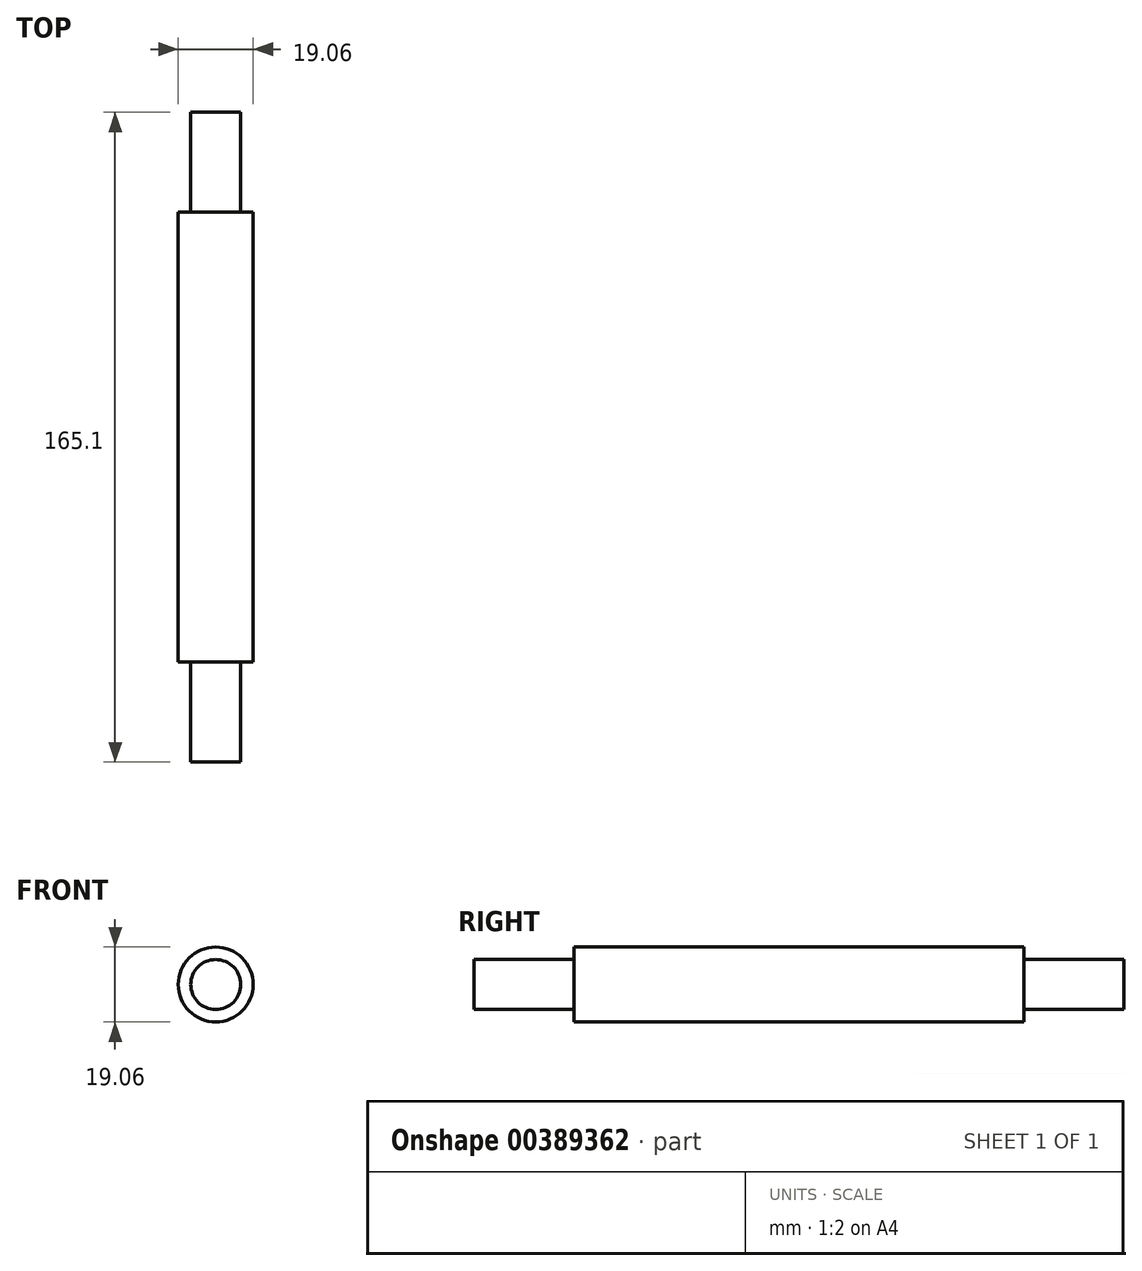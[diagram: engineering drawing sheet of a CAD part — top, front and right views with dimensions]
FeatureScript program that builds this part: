
annotation { "Feature Type Name" : "Feature", "Feature Type Description" : "" }
export const myFeature = defineFeature(function(context is Context, id is Id, definition is map)
    precondition{}
    {
        {
            var Q0;
            Q0=qCreatedBy(makeId("Front.planeOp"),FACE);
            var sketch = newSketch(context, id + "F0", { "sketchPlane" : qUnion([Q0])});
            skCircle(sketch, "E0", {"center": v(0, 0) * mm, "radius": 9.53 * mm});
            skSolve(sketch);
        }
        {
            var Q0;
            Q0=makeQuery(id+"F0.imprint","IMPRINT",FACE,{"disambiguationData":[TD([[makeQuery(id+"F0.imprint","IMPRINT",EDGE,{"derivedFrom":sQuery(id+"F0.wireOp",EDGE,"E0")}),1.0]])]});
            extrude(context, id + "F1", {"entities" : qUnion([Q0]), "depth" : 114.3 * mm});
        }
        {
            var Q0;
            Q0=makeQuery(id+"F1.opExtrude","CAP_FACE",FACE,{"disambiguationData":[OSD([sQuery(id+"F0.wireOp",EDGE,"E0")])],"isStart":false});
            var sketch = newSketch(context, id + "F2", { "sketchPlane" : qUnion([Q0])});
            skCircle(sketch, "E1", {"center": v(0, 0) * mm, "radius": 6.35 * mm});
            skSolve(sketch);
        }
        {
            var Q0;
            Q0 = qSketchRegion(id + "F2", true);
            extrude(context, id + "F3", {"entities" : qUnion([Q0]), "operationType" : NewBodyOperationType.ADD, "depth" : 25.4 * mm});
        }
        {
            var Q0;
            Q0=makeQuery(id+"F1.opExtrude","CAP_FACE",FACE,{"disambiguationData":[OSD([sQuery(id+"F0.wireOp",EDGE,"E0")])],"isStart":true});
            var sketch = newSketch(context, id + "F4", { "sketchPlane" : qUnion([Q0])});
            skCircle(sketch, "E2", {"center": v(0, 0) * mm, "radius": 6.35 * mm});
            skCircle(sketch, "E3", {"center": v(0, 0) * mm, "radius": 9.53 * mm});
            skSolve(sketch);
        }
        {
            var Q0;
            Q0=makeQuery(id+"F4.imprint","IMPRINT",FACE,{"disambiguationData":[TD([[makeQuery(id+"F4.imprint","IMPRINT",EDGE,{"derivedFrom":sQuery(id+"F4.wireOp",EDGE,"E2")}),1.0]])]});
            extrude(context, id + "F5", {"entities" : qUnion([Q0]), "operationType" : NewBodyOperationType.ADD, "depth" : 25.4 * mm});
        }
    });
